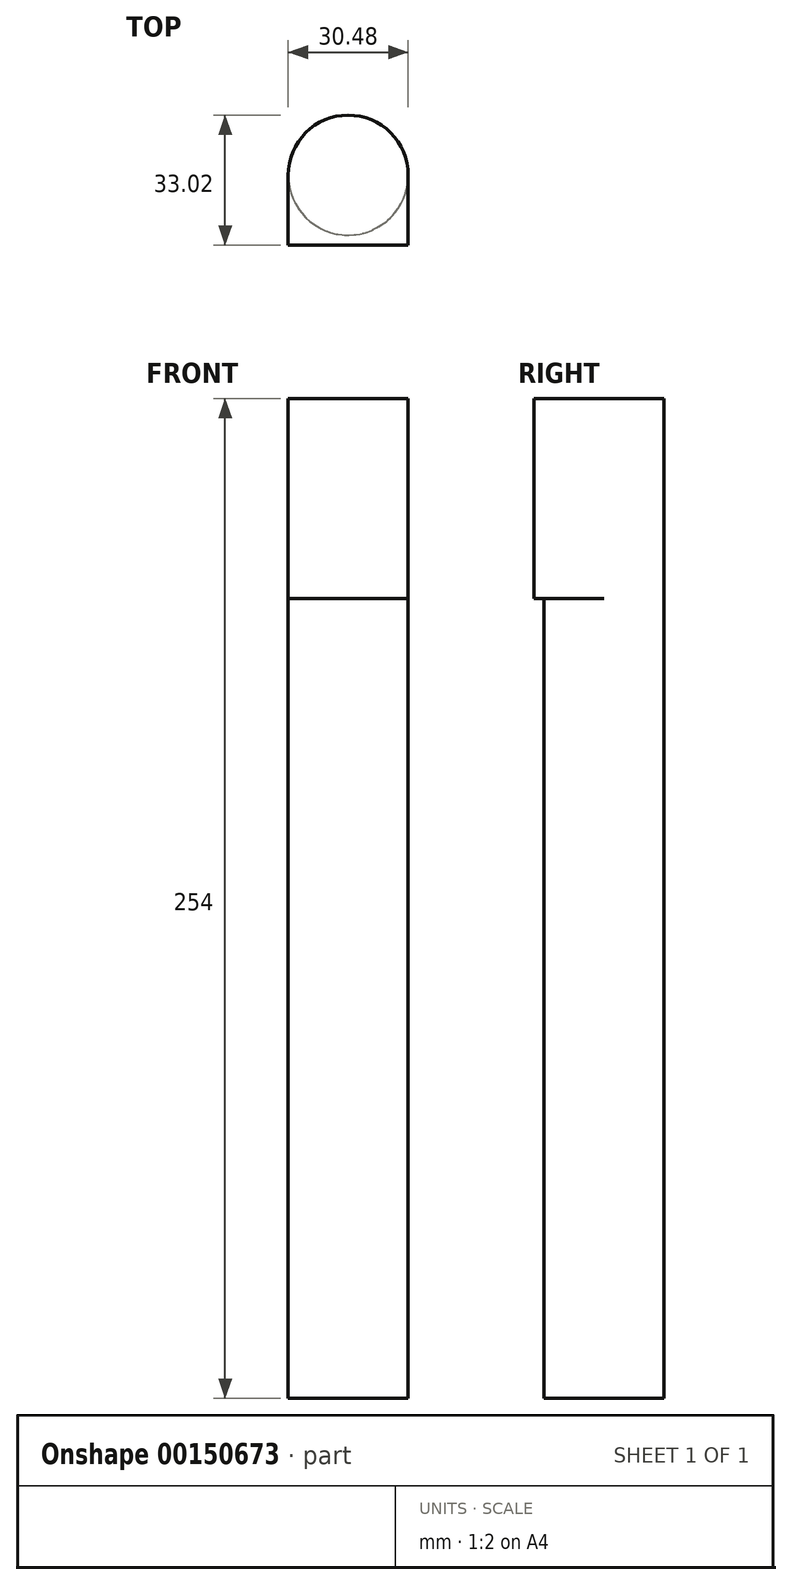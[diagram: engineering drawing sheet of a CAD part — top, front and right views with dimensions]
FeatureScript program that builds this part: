
annotation { "Feature Type Name" : "Feature", "Feature Type Description" : "" }
export const myFeature = defineFeature(function(context is Context, id is Id, definition is map)
    precondition{}
    {
        {
            var Q0;
            Q0=qCreatedBy(makeId("Top.planeOp"),FACE);
            var sketch = newSketch(context, id + "F0", { "sketchPlane" : qUnion([Q0])});
            skCircle(sketch, "E0", {"center": v(0, 0) * mm, "radius": 15.24 * mm});
            skSolve(sketch);
        }
        {
            var Q0;
            Q0=makeQuery(id+"F0.imprint","IMPRINT",FACE,{"disambiguationData":[TD([[makeQuery(id+"F0.imprint","IMPRINT",EDGE,{"derivedFrom":sQuery(id+"F0.wireOp",EDGE,"E0")}),1.0]])]});
            extrude(context, id + "F1", {"entities" : qUnion([Q0]), "depth" : 203.2 * mm});
        }
        {
            var Q0;
            Q0=makeQuery(id+"F1.opExtrude","CAP_FACE",FACE,{"disambiguationData":[OSD([sQuery(id+"F0.wireOp",EDGE,"E0")])],"isStart":false});
            var sketch = newSketch(context, id + "F3", { "sketchPlane" : qUnion([Q0])});
            skLineSegment(sketch, "E1.bottom", {"start": v(15.24, -17.78) * mm, "end": v(-15.24, -17.78) * mm});
            skLineSegment(sketch, "E1.top", {"start": v(15.24, 17.78) * mm, "end": v(-15.24, 17.78) * mm});
            skLineSegment(sketch, "E1.left", {"start": v(15.24, -17.78) * mm, "end": v(15.24, 17.78) * mm});
            skLineSegment(sketch, "E1.right", {"start": v(-15.24, -17.78) * mm, "end": v(-15.24, 17.78) * mm});
            skPoint(sketch, "E1.middle", {"position": v(0, 0) * mm});
            skSolve(sketch);
        }
        {
            var Q0;
            Q0=makeQuery(id+"F3.imprint","IMPRINT",FACE,{"disambiguationData":[TD([[makeQuery(id+"F3.imprint","IMPRINT",EDGE,{"derivedFrom":makeQuery(id+"F1.opExtrude","CAP_EDGE",EDGE,{"disambiguationData":[OSD([sQuery(id+"F0.wireOp",EDGE,"E0")])],"isStart":false})}),1.0]])]});
            var Q1;
            Q1=makeQuery(id+"F3.imprint","IMPRINT",FACE,{"disambiguationData":[TD([[makeQuery(id+"F3.imprint","IMPRINT",EDGE,{"derivedFrom":sQuery(id+"F3.wireOp",EDGE,"E1.bottom")}),-1.0]])]});
            extrude(context, id + "F4", {"entities" : qUnion([Q0, Q1]), "operationType" : NewBodyOperationType.ADD, "depth" : 50.8 * mm});
        }
    });
